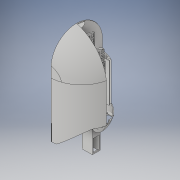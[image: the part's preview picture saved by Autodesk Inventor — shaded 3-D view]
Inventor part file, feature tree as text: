
AUTODESK INVENTOR PART (.ipt)
format: ipt  version: 2019 (Build 230136000, 136)  size: 1,873,408 bytes
history: native  units: mm
features: sketch x54, extrude x51, pattern_linear x10, projected_geometry x8, other x6, mirror x5, loft x3, fillet x2, shell x1
ambient origin geometry x8: Origin, YZ Plane, XZ Plane, XY Plane, X Axis, Y Axis, Z Axis, Center Point
bodies: Body1 (feature_tree)
feature tree (140):
  sketch  "Эскиз4"
  other  "РабПлоскость1"
  sketch  "Эскиз5"
  loft  "Лофт1"
  extrude  "Выдавливание2"  Depth=100.0mm
  shell  "Оболочка1"  Thickness=17.0mm
  sketch  "Эскиз21"
  extrude  "Выдавливание15"  Depth=4.0mm
  extrude  "Выдавливание16"  Depth=35.0mm
  other  "РабПлоскость7"
  sketch  "Эскиз23"
  extrude  "Выдавливание17"  TaperAngle=0.0deg  [1 undecoded]
  extrude  "Выдавливание18"  TaperAngle=0.0deg  [1 undecoded]
  sketch  "Эскиз24"
  extrude  "Выдавливание19"  TaperAngle=0.0deg  [1 undecoded]
  extrude  "Выдавливание20"  Depth=130.0mm TaperAngle=0.0deg
  extrude  "Выдавливание21"  Depth=5.0mm
  mirror  "Зеркальное отражение2"
  extrude  "Выдавливание22"  Depth=2.0mm
  extrude  "Выдавливание23"  Depth=2.0mm
  extrude  "Выдавливание24"  Depth=2.0mm
  extrude  "Выдавливание25"  Depth=20.0mm
  pattern_linear  "Прямоуг.массив1"  Spacing1=10.0mm  [1 undecoded]
  pattern_linear  "Прямоуг.массив2"  Spacing1=10.0mm  [1 undecoded]
  extrude  "Выдавливание26"  Depth=143.802871mm
  pattern_linear  "Прямоуг.массив3"  Spacing1=0.0mm  [1 undecoded]
  extrude  "Выдавливание27"  Depth=1.0mm TaperAngle=0.0deg
  pattern_linear  "Прямоуг.массив4"  Spacing1=5.0mm  [1 undecoded]
  extrude  "Выдавливание28"  Depth=5.0mm
  pattern_linear  "Прямоуг.массив5"  Spacing1=2.0mm  [1 undecoded]
  extrude  "Выдавливание29"  Depth=2.0mm
  pattern_linear  "Прямоуг.массив6"  Spacing1=5.0mm  [1 undecoded]
  extrude  "Выдавливание30"  Depth=1.0mm TaperAngle=0.0deg
  pattern_linear  "Прямоуг.массив7"  Spacing1=3.0mm  [1 undecoded]
  extrude  "Выдавливание31"  Depth=2.0mm
  pattern_linear  "Прямоуг.массив8"  Spacing1=6.0mm  [1 undecoded]
  extrude  "Выдавливание32"  Depth=1.0mm TaperAngle=0.0deg
  pattern_linear  "Прямоуг.массив9"  Spacing1=2.0mm  [1 undecoded]
  extrude  "Выдавливание33"  Depth=2.0mm
  pattern_linear  "Прямоуг.массив10"  Spacing1=2.0mm  [1 undecoded]
  mirror  "Зеркальное отражение3"
  extrude  "Выдавливание34"  Depth=5.0mm
  extrude  "Выдавливание35"  Depth=1.0mm TaperAngle=0.0deg
  extrude  "Выдавливание36"  Depth=30.0mm
  extrude  "Выдавливание37"  Depth=2.0mm
  fillet  "Сопряжение1"  Radius=30.0mm
  extrude  "Выдавливание38"  Depth=2.0mm
  sketch  "Эскиз44"
  sketch  "Эскиз45"
  mirror  "Зеркальное отражение4"
  extrude  "Выдавливание41"  Depth=1.0mm TaperAngle=0.0deg
  extrude  "Выдавливание42"  Depth=10.0mm
  extrude  "Выдавливание43"  Depth=6.0mm
  sketch  "Эскиз50"
  other  "РабПлоскость9"
  extrude  "Выдавливание44"  Depth=7.0mm
  sketch  "Эскиз52"
  extrude  "Выдавливание45"  Depth=14.0mm
  other  "РабПлоскость10"
  extrude  "Выдавливание49"  Depth=1.0mm TaperAngle=0.0deg
  extrude  "Выдавливание50"  Depth=14.0mm
  extrude  "Выдавливание51"  Depth=14.0mm
  extrude  "Выдавливание52"  Depth=7.0mm
  extrude  "Выдавливание53"  Depth=10.0mm
  extrude  "Выдавливание54"  Depth=3.0mm
  sketch  "Эскиз58"
  extrude  "Выдавливание55"  Depth=3.0mm
  extrude  "Выдавливание56"  Depth=1.0mm TaperAngle=0.0deg
  extrude  "Выдавливание57"  Depth=14.0mm
  extrude  "Выдавливание59"  Depth=14.0mm
  extrude  "Выдавливание61"  Depth=3.0mm
  loft  "Лофт3"
  fillet  "Сопряжение2"  Radius=7.0mm
  extrude  "Выдавливание62"  Depth=10.0mm
  mirror  "Зеркальное отражение5"
  other  "РабПлоскость11"
  loft  "Лофт4"
  sketch  "Эскиз76"
  extrude  "Выдавливание63"  Depth=15.0mm
  extrude  "Выдавливание64"  Depth=15.0mm
  extrude  "Выдавливание65"  Depth=7.0mm
  extrude  "Выдавливание66"  Depth=10.0mm
  extrude  "Выдавливание67"  Depth=5.0mm
  sketch  "Эскиз81"
  extrude  "Выдавливание68"  Depth=1.0mm TaperAngle=0.0deg
  extrude  "Выдавливание69"  Depth=15.0mm
  sketch  "Эскиз83"
  mirror  "Зеркальное отражение6"
  extrude  "Выдавливание70"  Depth=10.0mm
  extrude  "Выдавливание71"  Depth=7.0mm
  sketch  "Эскиз6"
  projected_geometry  "Спроецированная петля1"
  sketch  "Эскиз22"
  sketch  "Эскиз25"
  sketch  "Эскиз26"
  sketch  "Эскиз27"
  sketch  "Эскиз28"
  sketch  "Эскиз29"
  sketch  "Эскиз30"
  sketch  "Эскиз31"
  sketch  "Эскиз32"
  sketch  "Эскиз33"
  sketch  "Эскиз34"
  sketch  "Эскиз35"
  sketch  "Эскиз36"
  sketch  "Эскиз37"
  sketch  "Эскиз38"
  sketch  "Эскиз39"
  sketch  "Эскиз40"
  sketch  "Эскиз41"
  sketch  "Эскиз42"
  projected_geometry  "Спроецированная петля14"
  sketch  "Эскиз46"
  projected_geometry  "Спроецированная петля15"
  sketch  "Эскиз47"
  sketch  "Эскиз49"
  projected_geometry  "Спроецированная петля16"
  other  "РабПлоскость8"
  sketch  "Эскиз51"
  sketch  "Эскиз54"
  projected_geometry  "Спроецированная петля17"
  sketch  "Эскиз55"
  sketch  "Эскиз56"
  sketch  "Эскиз57"
  projected_geometry  "Спроецированная петля18"
  sketch  "Эскиз59"
  sketch  "Эскиз60"
  sketch  "Эскиз61"
  sketch  "Эскиз64"
  projected_geometry  "Спроецированная петля19"
  sketch  "Эскиз65"
  projected_geometry  "Спроецированная петля20"
  sketch  "Эскиз71"
  sketch  "Эскиз72"
  sketch  "Эскиз73"
  sketch  "Эскиз74"
  sketch  "Эскиз75"
  sketch  "Эскиз77"
  sketch  "Эскиз80"
  sketch  "Эскиз84"
note: 13 required parameter values undecoded (feature->parameter linkage not recoverable at this tier; creation-order binding heuristic only, values carry confidence <= 0.55)
